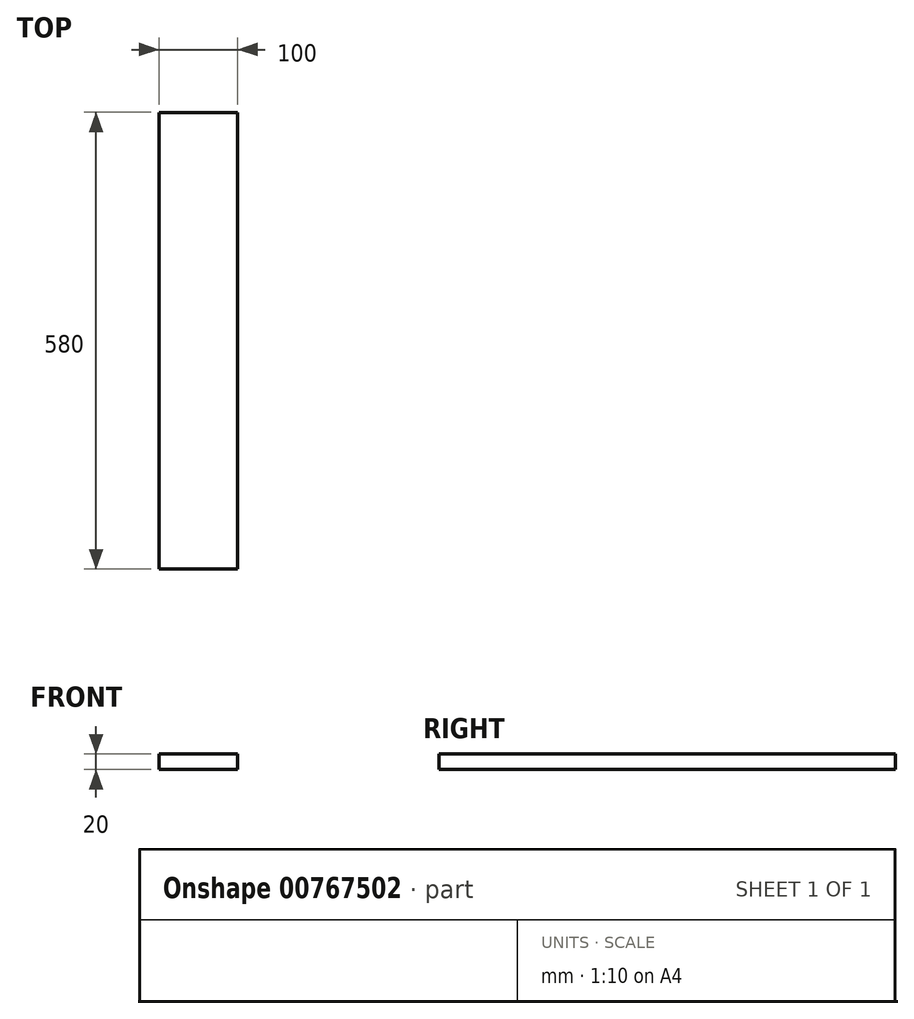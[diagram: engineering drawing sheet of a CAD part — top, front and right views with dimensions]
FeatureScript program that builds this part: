
annotation { "Feature Type Name" : "Feature", "Feature Type Description" : "" }
export const myFeature = defineFeature(function(context is Context, id is Id, definition is map)
    precondition{}
    {
        {
            var Q0;
            Q0=qCreatedBy(makeId("Top.planeOp"),FACE);
            var sketch = newSketch(context, id + "F0", { "sketchPlane" : qUnion([Q0])});
            skLineSegment(sketch, "E0", {"start": v(-16.53, -41.93) * mm, "end": v(83.47, -41.93) * mm});
            skLineSegment(sketch, "E1", {"start": v(83.47, -41.93) * mm, "end": v(83.47, 538.07) * mm});
            skLineSegment(sketch, "E2", {"start": v(83.47, 538.07) * mm, "end": v(-16.53, 538.07) * mm});
            skLineSegment(sketch, "E3", {"start": v(-16.53, 538.07) * mm, "end": v(-16.53, -41.93) * mm});
            skSolve(sketch);
        }
        {
            var Q0;
            Q0 = qSketchRegion(id + "F0", true);
            extrude(context, id + "F1", {"entities" : qUnion([Q0]), "depth" : 20 * mm, "offsetDistance" : 25 * mm});
        }
    });
